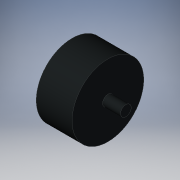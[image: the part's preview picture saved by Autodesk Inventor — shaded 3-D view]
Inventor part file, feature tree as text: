
AUTODESK INVENTOR PART (.ipt)
format: ipt  version: 2019 (Build 230136000, 136)  size: 116,736 bytes
history: native  units: mm
features: other x7, revolve x1, sketch x1
ambient origin geometry x8: Origin, YZ Plane, XZ Plane, XY Plane, X Axis, Y Axis, Z Axis, Center Point
bodies: Solid1 (feature_tree)
feature tree (9):
  revolve  "Revolution1"  [1 undecoded]
  other  "p1_XY"
  other  "p1_YZ"
  other  "p1_ZX"
  other  "p1_X"
  other  "p1_Y"
  other  "p1_Z"
  other  "p1_Center"
  sketch  "Sketch_1"  dims[d0=360.0deg]
note: 1 required parameter value undecoded (feature->parameter linkage not recoverable at this tier; creation-order binding heuristic only, values carry confidence <= 0.55)
